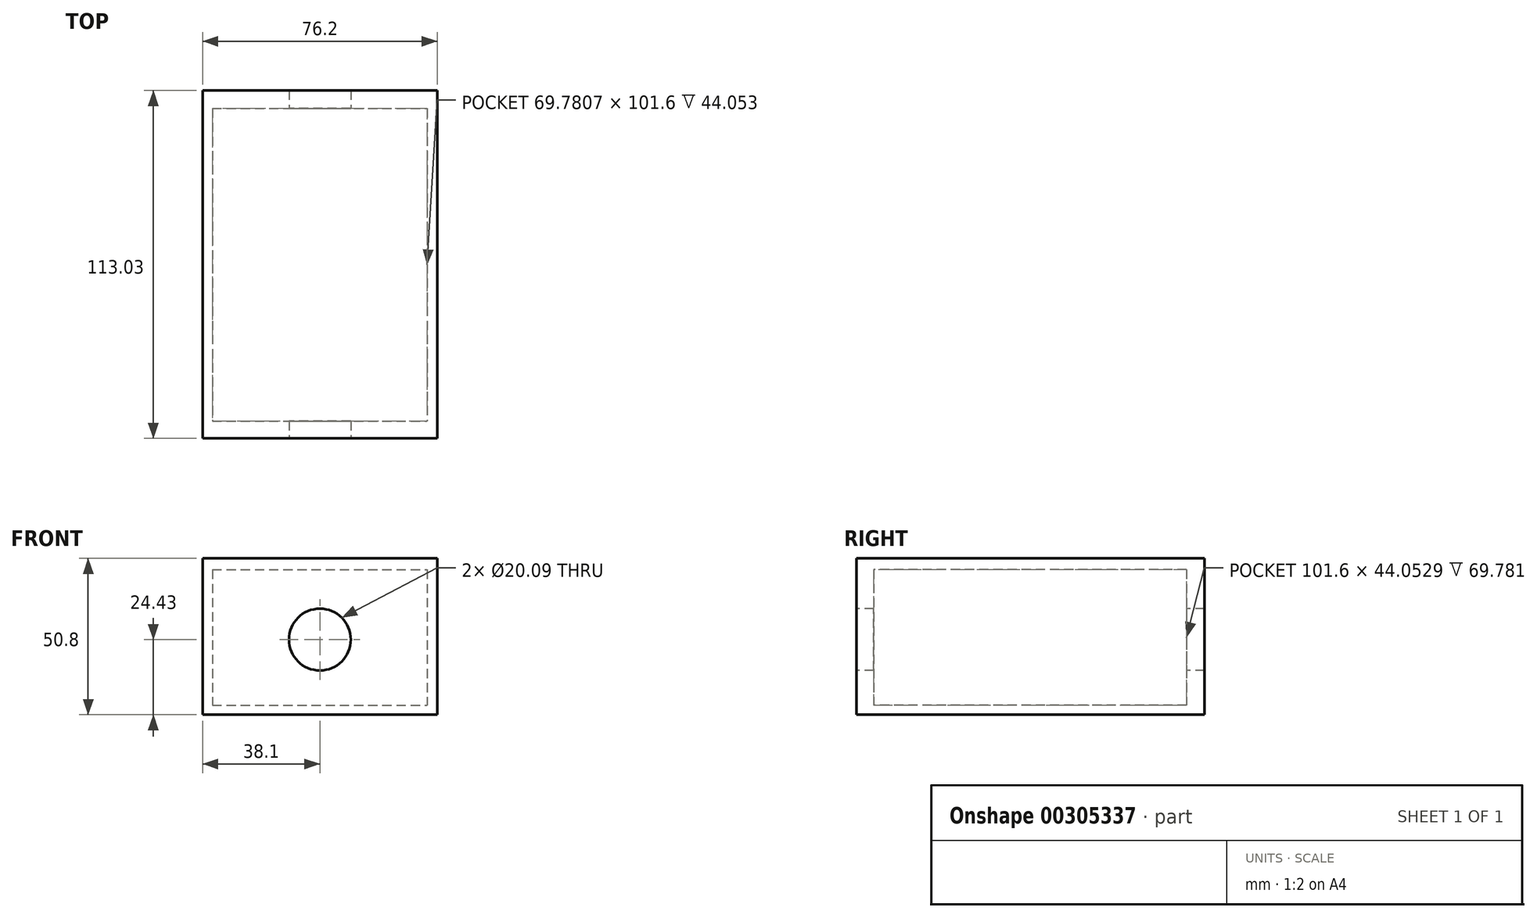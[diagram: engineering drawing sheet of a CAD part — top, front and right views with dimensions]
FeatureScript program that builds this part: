
annotation { "Feature Type Name" : "Feature", "Feature Type Description" : "" }
export const myFeature = defineFeature(function(context is Context, id is Id, definition is map)
    precondition{}
    {
        {
            var Q0;
            Q0=qCreatedBy(makeId("Top.planeOp"),FACE);
            var sketch = newSketch(context, id + "F0", { "sketchPlane" : qUnion([Q0])});
            skLineSegment(sketch, "E0.bottom", {"start": v(38.1, 50.8) * mm, "end": v(-38.1, 50.8) * mm});
            skLineSegment(sketch, "E0.top", {"start": v(38.1, -50.8) * mm, "end": v(-38.1, -50.8) * mm});
            skLineSegment(sketch, "E0.left", {"start": v(38.1, 50.8) * mm, "end": v(38.1, -50.8) * mm});
            skLineSegment(sketch, "E0.right", {"start": v(-38.1, 50.8) * mm, "end": v(-38.1, -50.8) * mm});
            skPoint(sketch, "E0.middle", {"position": v(0, 0) * mm});
            skSolve(sketch);
        }
        {
            var Q0;
            Q0=makeQuery(id+"F0.imprint","IMPRINT",FACE,{"disambiguationData":[TD([[makeQuery(id+"F0.imprint","IMPRINT",EDGE,{"derivedFrom":sQuery(id+"F0.wireOp",EDGE,"E0.bottom")}),1.0]])]});
            extrude(context, id + "F1", {"entities" : qUnion([Q0]), "depth" : 50.8 * mm});
        }
        {
            var Q0;
            Q0=makeQuery(id+"F1.opExtrude","SWEPT_FACE",FACE,{"disambiguationData":[OSD([sQuery(id+"F0.wireOp",EDGE,"E0.top")])]});
            var sketch = newSketch(context, id + "F2", { "sketchPlane" : qUnion([Q0])});
            skLineSegment(sketch, "E1.bottom", {"start": v(-34.9, 47.12) * mm, "end": v(34.89, 47.12) * mm});
            skLineSegment(sketch, "E1.top", {"start": v(-34.9, 3.07) * mm, "end": v(34.89, 3.07) * mm});
            skLineSegment(sketch, "E1.left", {"start": v(-34.9, 47.12) * mm, "end": v(-34.9, 3.07) * mm});
            skLineSegment(sketch, "E1.right", {"start": v(34.89, 47.12) * mm, "end": v(34.89, 3.07) * mm});
            skSolve(sketch);
        }
        {
            var Q0;
            Q0 = qSketchRegion(id + "F2", true);
            extrude(context, id + "F3", {"entities" : qUnion([Q0]), "operationType" : NewBodyOperationType.REMOVE, "oppositeDirection" : true, "depth" : 159.77 * mm});
        }
        {
            var Q0;
            Q0=makeQuery(id+"F1.opExtrude","SWEPT_FACE",FACE,{"disambiguationData":[OSD([sQuery(id+"F0.wireOp",EDGE,"E0.top")])]});
            var sketch = newSketch(context, id + "F4", { "sketchPlane" : qUnion([Q0])});
            skLineSegment(sketch, "E2.bottom", {"start": v(-38.1, 0) * mm, "end": v(38.1, 0) * mm});
            skLineSegment(sketch, "E2.top", {"start": v(-38.1, 50.8) * mm, "end": v(38.1, 50.8) * mm});
            skLineSegment(sketch, "E2.left", {"start": v(-38.1, 0) * mm, "end": v(-38.1, 50.8) * mm});
            skLineSegment(sketch, "E2.right", {"start": v(38.1, 0) * mm, "end": v(38.1, 50.8) * mm});
            skSolve(sketch);
        }
        {
            var Q0;
            Q0 = qSketchRegion(id + "F4", true);
            extrude(context, id + "F5", {"entities" : qUnion([Q0]), "operationType" : NewBodyOperationType.ADD, "depth" : 5.6 * mm});
        }
        {
            var Q0;
            Q0=makeQuery(id+"F1.opExtrude","SWEPT_FACE",FACE,{"disambiguationData":[OSD([sQuery(id+"F0.wireOp",EDGE,"E0.bottom")])]});
            var sketch = newSketch(context, id + "F6", { "sketchPlane" : qUnion([Q0])});
            skLineSegment(sketch, "E3.bottom", {"start": v(-38.1, 50.8) * mm, "end": v(38.1, 50.8) * mm});
            skLineSegment(sketch, "E3.top", {"start": v(-38.1, 0) * mm, "end": v(38.1, 0) * mm});
            skLineSegment(sketch, "E3.left", {"start": v(-38.1, 50.8) * mm, "end": v(-38.1, 0) * mm});
            skLineSegment(sketch, "E3.right", {"start": v(38.1, 50.8) * mm, "end": v(38.1, 0) * mm});
            skSolve(sketch);
        }
        {
            var Q0;
            Q0 = qSketchRegion(id + "F6", true);
            extrude(context, id + "F7", {"entities" : qUnion([Q0]), "operationType" : NewBodyOperationType.ADD, "depth" : 5.84 * mm});
        }
        {
            var Q0;
            Q0=makeQuery(id+"F5.opExtrude","CAP_FACE",FACE,{"disambiguationData":[OSD([sQuery(id+"F4.wireOp",EDGE,"E2.bottom"),sQuery(id+"F4.wireOp",EDGE,"E2.top"),sQuery(id+"F4.wireOp",EDGE,"E2.left"),sQuery(id+"F4.wireOp",EDGE,"E2.right")])],"isStart":false});
            var sketch = newSketch(context, id + "F8", { "sketchPlane" : qUnion([Q0])});
            skCircle(sketch, "E4", {"center": v(0, 24.43) * mm, "radius": 10.04 * mm});
            skSolve(sketch);
        }
        {
            var Q0;
            Q0 = qSketchRegion(id + "F8", true);
            extrude(context, id + "F9", {"entities" : qUnion([Q0]), "operationType" : NewBodyOperationType.REMOVE, "oppositeDirection" : true, "depth" : 166.12 * mm});
        }
    });
